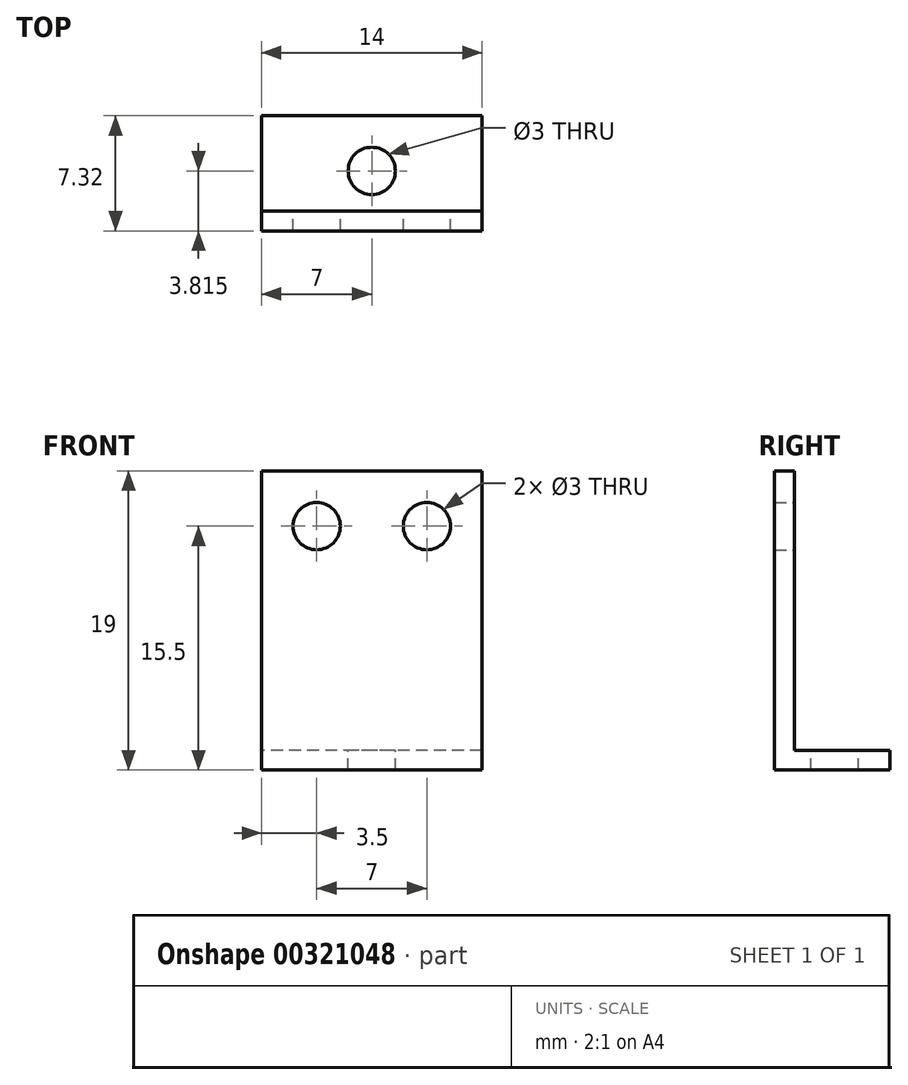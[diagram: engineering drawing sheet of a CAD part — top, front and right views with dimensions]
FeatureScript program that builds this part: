
annotation { "Feature Type Name" : "Feature", "Feature Type Description" : "" }
export const myFeature = defineFeature(function(context is Context, id is Id, definition is map)
    precondition{}
    {
        {
            var Q0;
            Q0=qCreatedBy(makeId("Front.planeOp"),FACE);
            var sketch = newSketch(context, id + "F0", { "sketchPlane" : qUnion([Q0])});
            skLineSegment(sketch, "E0.bottom", {"start": v(7, 9.5) * mm, "end": v(-7, 9.5) * mm});
            skLineSegment(sketch, "E0.top", {"start": v(7, -9.5) * mm, "end": v(-7, -9.5) * mm});
            skLineSegment(sketch, "E0.left", {"start": v(7, 9.5) * mm, "end": v(7, -9.5) * mm});
            skLineSegment(sketch, "E0.right", {"start": v(-7, 9.5) * mm, "end": v(-7, -9.5) * mm});
            skPoint(sketch, "E0.middle", {"position": v(0, 0) * mm});
            skSolve(sketch);
        }
        {
            var Q0;
            Q0 = qSketchRegion(id + "F0", true);
            extrude(context, id + "F1", {"entities" : qUnion([Q0]), "depth" : 1.25 * mm});
        }
        {
            var Q0;
            Q0=makeQuery(id+"F1.opExtrude","CAP_FACE",FACE,{"disambiguationData":[OSD([sQuery(id+"F0.wireOp",EDGE,"E0.bottom"),sQuery(id+"F0.wireOp",EDGE,"E0.top"),sQuery(id+"F0.wireOp",EDGE,"E0.left"),sQuery(id+"F0.wireOp",EDGE,"E0.right")])],"isStart":true});
            var sketch = newSketch(context, id + "F2", { "sketchPlane" : qUnion([Q0])});
            skLineSegment(sketch, "E1.bottom", {"start": v(-7, -9.5) * mm, "end": v(7, -9.5) * mm});
            skLineSegment(sketch, "E1.top", {"start": v(-7, -8.25) * mm, "end": v(7, -8.25) * mm});
            skLineSegment(sketch, "E1.left", {"start": v(-7, -9.5) * mm, "end": v(-7, -8.25) * mm});
            skLineSegment(sketch, "E1.right", {"start": v(7, -9.5) * mm, "end": v(7, -8.25) * mm});
            skSolve(sketch);
        }
        {
            var Q0;
            Q0 = qSketchRegion(id + "F2", true);
            extrude(context, id + "F3", {"entities" : qUnion([Q0]), "operationType" : NewBodyOperationType.ADD, "depth" : 17.75 * mm});
        }
        {
            var Q0;
            Q0=makeQuery(id+"F1.opExtrude","CAP_FACE",FACE,{"disambiguationData":[OSD([sQuery(id+"F0.wireOp",EDGE,"E0.bottom"),sQuery(id+"F0.wireOp",EDGE,"E0.top"),sQuery(id+"F0.wireOp",EDGE,"E0.left"),sQuery(id+"F0.wireOp",EDGE,"E0.right")])],"isStart":true});
            var sketch = newSketch(context, id + "F4", { "sketchPlane" : qUnion([Q0])});
            skCircle(sketch, "E2", {"center": v(-3.5, 6) * mm, "radius": 1.5 * mm});
            skCircle(sketch, "E3", {"center": v(3.5, 6) * mm, "radius": 1.5 * mm});
            skSolve(sketch);
        }
        {
            var Q0;
            Q0 = qSketchRegion(id + "F4", true);
            extrude(context, id + "F5", {"entities" : qUnion([Q0]), "operationType" : NewBodyOperationType.REMOVE, "oppositeDirection" : true, "depth" : 25 * mm});
        }
        {
            var Q0;
            Q0=makeQuery(id+"F3.opExtrude","SWEPT_FACE",FACE,{"disambiguationData":[OSD([sQuery(id+"F2.wireOp",EDGE,"E1.top")])]});
            var sketch = newSketch(context, id + "F6", { "sketchPlane" : qUnion([Q0])});
            skCircle(sketch, "E4", {"center": v(0, 2.57) * mm, "radius": 1.5 * mm});
            skSolve(sketch);
        }
        {
            var Q0;
            Q0 = qSketchRegion(id + "F6", true);
            extrude(context, id + "F7", {"entities" : qUnion([Q0]), "operationType" : NewBodyOperationType.REMOVE, "oppositeDirection" : true, "depth" : 25 * mm});
        }
        {
            var Q0;
            Q0=makeQuery(id+"F3.opExtrude","SWEPT_FACE",FACE,{"disambiguationData":[OSD([sQuery(id+"F2.wireOp",EDGE,"E1.top")])]});
            var sketch = newSketch(context, id + "F8", { "sketchPlane" : qUnion([Q0])});
            skLineSegment(sketch, "E5.bottom", {"start": v(-7, 17.75) * mm, "end": v(7, 17.75) * mm});
            skLineSegment(sketch, "E5.top", {"start": v(-7, 6.07) * mm, "end": v(7, 6.07) * mm});
            skLineSegment(sketch, "E5.left", {"start": v(-7, 17.75) * mm, "end": v(-7, 6.07) * mm});
            skLineSegment(sketch, "E5.right", {"start": v(7, 17.75) * mm, "end": v(7, 6.07) * mm});
            skSolve(sketch);
        }
        {
            var Q0;
            Q0 = qSketchRegion(id + "F8", true);
            extrude(context, id + "F9", {"entities" : qUnion([Q0]), "operationType" : NewBodyOperationType.REMOVE, "oppositeDirection" : true, "depth" : 25 * mm});
        }
    });
